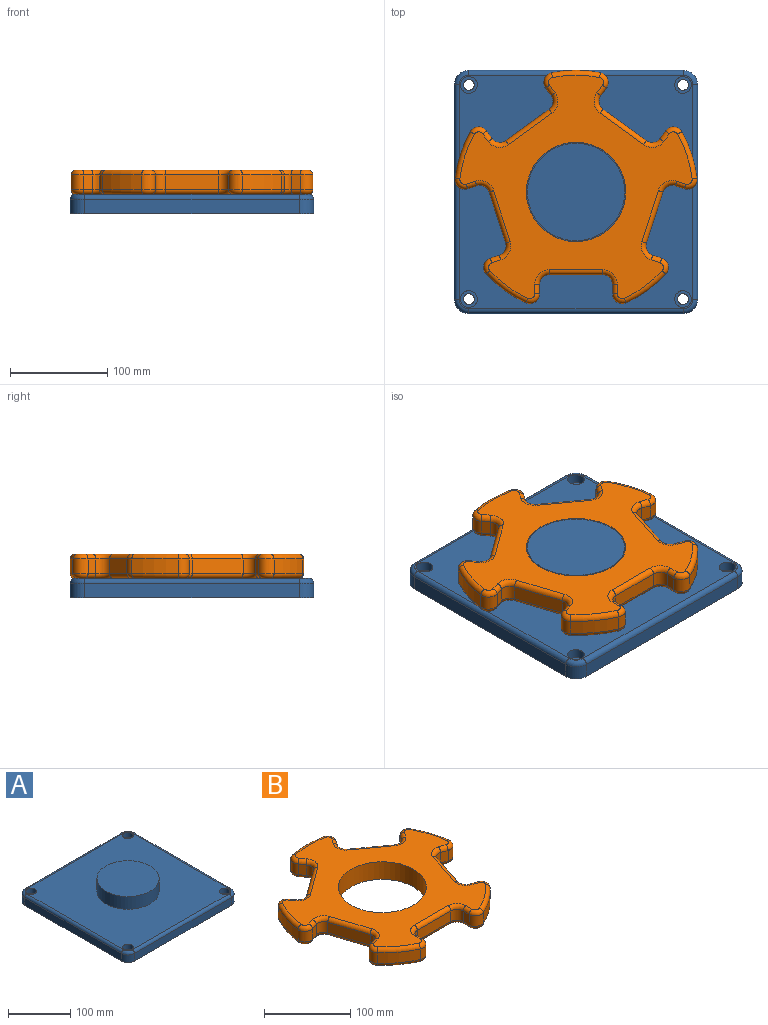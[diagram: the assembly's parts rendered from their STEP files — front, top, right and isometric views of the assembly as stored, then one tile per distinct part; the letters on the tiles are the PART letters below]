
ASSEMBLY  parts=2 mates=1
PART A: 32 faces, bbox 252.5x252.5x45 mm
  f0: plane 220x15mm, normal (1,0,0), area 3300mm2, adj f5,f8,f11,f27
  f1: plane 220x15mm, normal (0,1,0), area 3300mm2, adj f5,f8,f9,f31
  f2: plane 220x15mm, normal (-1,0,0), area 3300mm2, adj f5,f9,f10,f28
  f3: plane 220x15mm, normal (0,-1,0), area 3300mm2, adj f5,f10,f11,f24
  f4: plane 240x240mm, normal (0,0,1), area 48725.4mm2, adj f6,f14,f17,f20,f23,f24,f25,f26
  f5: plane 250x250mm, normal (0,0,-1), area 61926.7mm2, adj f0,f1,f2,f3,f8,f9,f10,f11
  f6: cylinder r=50mm len=100mm, axis (0,0,-1), area 7854mm2, adj f4,f7
  f7: plane 100x100mm, normal (0,0,1), area 7854mm2, adj f6
  f8: cylinder r=15mm len=15mm, axis (0,0,-1), area 353.4mm2, adj f0,f1,f5,f29
  f9: cylinder r=15mm len=15mm, axis (0,0,1), area 353.4mm2, adj f1,f2,f5,f30
  f10: cylinder r=15mm len=15mm, axis (0,0,-1), area 353.4mm2, adj f2,f3,f5,f26
  f11: cylinder r=15mm len=15mm, axis (0,0,1), area 353.4mm2, adj f0,f3,f5,f25
  f12: cylinder r=5.5mm len=11mm, axis (0,0,1), area 345.6mm2, adj f5,f13
  f13: plane 17.25x17.25mm, normal (0,0,1), area 138.7mm2, adj f12,f14
  f14: cylinder r=8.62mm len=17.25mm, axis (0,0,1), area 541.9mm2, adj f4,f13
  f15: cylinder r=5.5mm len=11mm, axis (0,0,1), area 345.6mm2, adj f5,f16
  f16: plane 17.25x17.25mm, normal (0,0,1), area 138.7mm2, adj f15,f17
  f17: cylinder r=8.62mm len=17.25mm, axis (0,0,1), area 541.9mm2, adj f4,f16
  f18: cylinder r=5.5mm len=11mm, axis (0,0,1), area 345.6mm2, adj f5,f19
  f19: plane 17.25x17.25mm, normal (0,0,1), area 138.7mm2, adj f18,f20
  f20: cylinder r=8.62mm len=17.25mm, axis (0,0,1), area 541.9mm2, adj f4,f19
  f21: cylinder r=5.5mm len=11mm, axis (0,0,1), area 345.6mm2, adj f5,f22
  f22: plane 17.25x17.25mm, normal (0,0,1), area 138.7mm2, adj f21,f23
  f23: cylinder r=8.62mm len=17.25mm, axis (0,0,1), area 541.9mm2, adj f4,f22
  f24: cylinder r=5mm len=220mm, axis (-1,0,0), area 1727.9mm2, adj f3,f4,f25,f26
  f25: torus R=10mm, axis (0,0,1), area 162.6mm2, adj f4,f11,f24,f27
  f26: torus R=10mm, axis (0,0,1), area 162.6mm2, adj f4,f10,f24,f28
  f27: cylinder r=5mm len=220mm, axis (0,-1,0), area 1727.9mm2, adj f0,f4,f25,f29
  f28: cylinder r=5mm len=220mm, axis (0,1,0), area 1727.9mm2, adj f2,f4,f26,f30
  f29: torus R=10mm, axis (0,0,1), area 162.6mm2, adj f4,f8,f27,f31
  f30: torus R=10mm, axis (0,0,1), area 162.6mm2, adj f4,f9,f28,f31
  f31: cylinder r=5mm len=220mm, axis (1,0,0), area 1727.9mm2, adj f1,f4,f29,f30
PART B: 123 faces, bbox 268.9x258.5x25 mm
  f0: plane 238.57x229.73mm, normal (0,0,1), area 21505.7mm2, adj f6,f83,f84,f85,f86,f87,f88,f89
  f1: plane 238.57x229.73mm, normal (0,0,-1), area 21505.7mm2, adj f6,f43,f44,f45,f46,f47,f48,f49
  f2: cylinder r=125mm len=47.82mm, axis (0,0,-1), area 759.5mm2, adj f34,f42,f74,f114
  f3: cylinder r=125mm len=50.29mm, axis (0,0,-1), area 759.5mm2, adj f27,f35,f75,f115
  f4: cylinder r=125mm len=47.82mm, axis (0,0,-1), area 759.5mm2, adj f20,f28,f59,f99
  f5: cylinder r=125mm len=40.68mm, axis (0,0,-1), area 759.5mm2, adj f13,f21,f43,f83
  f6: cylinder r=51mm len=102mm, axis (0,0,-1), area 8011.1mm2, adj f0,f1
  f7: cylinder r=125mm len=40.68mm, axis (0,0,-1), area 759.5mm2, adj f14,f41,f58,f98
  f8: plane 15x9.73mm, normal (-1,0,0), area 146mm2, adj f11,f14,f54,f94
  f9: plane 55x15mm, normal (0,-1,0), area 825mm2, adj f11,f12,f50,f90
  f10: plane 15x9.73mm, normal (1,0,0), area 146mm2, adj f12,f13,f46,f86
  f11: cylinder r=10mm len=15mm, axis (0,0,-1), area 235.6mm2, adj f8,f9,f52,f92
  f12: cylinder r=10mm len=15mm, axis (0,0,-1), area 235.6mm2, adj f9,f10,f48,f88
  f13: cylinder r=10mm len=15mm, axis (0,0,-1), area 299.5mm2, adj f5,f10,f44,f84
  f14: cylinder r=10mm len=15mm, axis (0,0,-1), area 299.5mm2, adj f7,f8,f56,f96
  f15: plane 15x9.26mm, normal (-0.31,0.95,0), area 146mm2, adj f18,f21,f47,f87
  f16: plane 52.31x17mm, normal (-0.95,-0.31,0), area 825mm2, adj f18,f19,f51,f91
  f17: plane 15x9.26mm, normal (0.31,-0.95,0), area 146mm2, adj f19,f20,f55,f95
  f18: cylinder r=10mm len=15mm, axis (0,0,-1), area 235.6mm2, adj f15,f16,f49,f89
  f19: cylinder r=10mm len=15mm, axis (0,0,-1), area 235.6mm2, adj f16,f17,f53,f93
  f20: cylinder r=10mm len=15mm, axis (0,0,-1), area 299.5mm2, adj f4,f17,f57,f97
  f21: cylinder r=10mm len=16.25mm, axis (0,0,-1), area 299.5mm2, adj f5,f15,f45,f85
  f22: plane 15x7.87mm, normal (0.81,0.59,0), area 146mm2, adj f25,f28,f63,f103
  f23: plane 44.5x32.33mm, normal (-0.59,0.81,0), area 825mm2, adj f25,f26,f67,f107
  f24: plane 15x7.87mm, normal (-0.81,-0.59,0), area 146mm2, adj f26,f27,f71,f111
  f25: cylinder r=10mm len=15mm, axis (0,0,-1), area 235.6mm2, adj f22,f23,f65,f105
  f26: cylinder r=10mm len=15mm, axis (0,0,-1), area 235.6mm2, adj f23,f24,f69,f109
  f27: cylinder r=10mm len=15.67mm, axis (0,0,-1), area 299.5mm2, adj f3,f24,f73,f113
  f28: cylinder r=10mm len=16.78mm, axis (0,0,-1), area 299.5mm2, adj f4,f22,f61,f101
  f29: plane 15x7.87mm, normal (0.81,-0.59,0), area 146mm2, adj f32,f35,f79,f119
  f30: plane 44.5x32.33mm, normal (0.59,0.81,0), area 825mm2, adj f32,f33,f82,f122
  f31: plane 15x7.87mm, normal (-0.81,0.59,0), area 146mm2, adj f33,f34,f78,f118
  f32: cylinder r=10mm len=15mm, axis (0,0,-1), area 235.6mm2, adj f29,f30,f81,f121
  f33: cylinder r=10mm len=15mm, axis (0,0,-1), area 235.6mm2, adj f30,f31,f80,f120
  f34: cylinder r=10mm len=16.78mm, axis (0,0,-1), area 299.5mm2, adj f2,f31,f76,f116
  f35: cylinder r=10mm len=15.67mm, axis (0,0,-1), area 299.5mm2, adj f3,f29,f77,f117
  f36: plane 15x9.26mm, normal (-0.31,-0.95,0), area 146mm2, adj f39,f42,f70,f110
  f37: plane 52.31x17mm, normal (0.95,-0.31,0), area 825mm2, adj f39,f40,f66,f106
  f38: plane 15x9.26mm, normal (0.31,0.95,0), area 146mm2, adj f40,f41,f62,f102
  f39: cylinder r=10mm len=15mm, axis (0,0,-1), area 235.6mm2, adj f36,f37,f68,f108
  f40: cylinder r=10mm len=15mm, axis (0,0,-1), area 235.6mm2, adj f37,f38,f64,f104
  f41: cylinder r=10mm len=16.25mm, axis (0,0,-1), area 299.5mm2, adj f7,f38,f60,f100
  f42: cylinder r=10mm len=15mm, axis (0,0,-1), area 299.5mm2, adj f2,f36,f72,f112
  f43: torus R=120mm, axis (0,0,1), area 391.9mm2, adj f1,f5,f44,f45
  f44: torus R=5mm, axis (0,0,1), area 128.3mm2, adj f1,f13,f43,f46
  f45: torus R=5mm, axis (0,0,1), area 128.3mm2, adj f1,f21,f43,f47
  f46: cylinder r=5mm len=9.73mm, axis (0,-1,0), area 76.4mm2, adj f1,f10,f44,f48
  f47: cylinder r=5mm len=10.8mm, axis (0.95,0.31,0), area 76.4mm2, adj f1,f15,f45,f49
  f48: torus R=15mm, axis (0,0,1), area 145.8mm2, adj f1,f12,f46,f50
  f49: torus R=15mm, axis (0,0,1), area 145.8mm2, adj f1,f18,f47,f51
  f50: cylinder r=5mm len=55mm, axis (-1,0,0), area 432mm2, adj f1,f9,f48,f52
  f51: cylinder r=5mm len=53.85mm, axis (-0.31,0.95,0), area 432mm2, adj f1,f16,f49,f53
  f52: torus R=15mm, axis (0,0,1), area 145.8mm2, adj f1,f11,f50,f54
  f53: torus R=15mm, axis (0,0,1), area 145.8mm2, adj f1,f19,f51,f55
  f54: cylinder r=5mm len=9.73mm, axis (0,1,0), area 76.4mm2, adj f1,f8,f52,f56
  f55: cylinder r=5mm len=10.8mm, axis (-0.95,-0.31,0), area 76.4mm2, adj f1,f17,f53,f57
  f56: torus R=5mm, axis (0,0,1), area 128.3mm2, adj f1,f14,f54,f58
  f57: torus R=5mm, axis (0,0,1), area 128.3mm2, adj f1,f20,f55,f59
  f58: torus R=120mm, axis (0,0,1), area 391.9mm2, adj f1,f7,f56,f60
  f59: torus R=120mm, axis (0,0,1), area 391.9mm2, adj f1,f4,f57,f61
  f60: torus R=5mm, axis (0,0,1), area 128.3mm2, adj f1,f41,f58,f62
  f61: torus R=5mm, axis (0,0,1), area 128.3mm2, adj f1,f28,f59,f63
  f62: cylinder r=5mm len=10.8mm, axis (0.95,-0.31,0), area 76.4mm2, adj f1,f38,f60,f64
  f63: cylinder r=5mm len=10.81mm, axis (0.59,-0.81,0), area 76.4mm2, adj f1,f22,f61,f65
  f64: torus R=15mm, axis (0,0,1), area 145.8mm2, adj f1,f40,f62,f66
  f65: torus R=15mm, axis (0,0,1), area 145.8mm2, adj f1,f25,f63,f67
  f66: cylinder r=5mm len=53.85mm, axis (-0.31,-0.95,0), area 432mm2, adj f1,f37,f64,f68
  f67: cylinder r=5mm len=47.44mm, axis (0.81,0.59,0), area 432mm2, adj f1,f23,f65,f69
  f68: torus R=15mm, axis (0,0,1), area 145.8mm2, adj f1,f39,f66,f70
  f69: torus R=15mm, axis (0,0,1), area 145.8mm2, adj f1,f26,f67,f71
  f70: cylinder r=5mm len=10.8mm, axis (-0.95,0.31,0), area 76.4mm2, adj f1,f36,f68,f72
  f71: cylinder r=5mm len=10.81mm, axis (-0.59,0.81,0), area 76.4mm2, adj f1,f24,f69,f73
  f72: torus R=5mm, axis (0,0,1), area 128.3mm2, adj f1,f42,f70,f74
  f73: torus R=5mm, axis (0,0,1), area 128.3mm2, adj f1,f27,f71,f75
  f74: torus R=120mm, axis (0,0,1), area 391.9mm2, adj f1,f2,f72,f76
  f75: torus R=120mm, axis (0,0,1), area 391.9mm2, adj f1,f3,f73,f77
  f76: torus R=5mm, axis (0,0,1), area 128.3mm2, adj f1,f34,f74,f78
  f77: torus R=5mm, axis (0,0,1), area 128.3mm2, adj f1,f35,f75,f79
  f78: cylinder r=5mm len=10.81mm, axis (0.59,0.81,0), area 76.4mm2, adj f1,f31,f76,f80
  f79: cylinder r=5mm len=10.81mm, axis (-0.59,-0.81,0), area 76.4mm2, adj f1,f29,f77,f81
  f80: torus R=15mm, axis (0,0,1), area 145.8mm2, adj f1,f33,f78,f82
  f81: torus R=15mm, axis (0,0,1), area 145.8mm2, adj f1,f32,f79,f82
  f82: cylinder r=5mm len=47.44mm, axis (0.81,-0.59,0), area 432mm2, adj f1,f30,f80,f81
  f83: torus R=120mm, axis (0,0,1), area 391.9mm2, adj f0,f5,f84,f85
  f84: torus R=5mm, axis (0,0,1), area 128.3mm2, adj f0,f13,f83,f86
  f85: torus R=5mm, axis (0,0,1), area 128.3mm2, adj f0,f21,f83,f87
  f86: cylinder r=5mm len=9.73mm, axis (0,1,0), area 76.4mm2, adj f0,f10,f84,f88
  f87: cylinder r=5mm len=10.8mm, axis (-0.95,-0.31,0), area 76.4mm2, adj f0,f15,f85,f89
  f88: torus R=15mm, axis (0,0,1), area 145.8mm2, adj f0,f12,f86,f90
  f89: torus R=15mm, axis (0,0,1), area 145.8mm2, adj f0,f18,f87,f91
  f90: cylinder r=5mm len=55mm, axis (1,0,0), area 432mm2, adj f0,f9,f88,f92
  f91: cylinder r=5mm len=53.85mm, axis (0.31,-0.95,0), area 432mm2, adj f0,f16,f89,f93
  f92: torus R=15mm, axis (0,0,1), area 145.8mm2, adj f0,f11,f90,f94
  f93: torus R=15mm, axis (0,0,1), area 145.8mm2, adj f0,f19,f91,f95
  f94: cylinder r=5mm len=9.73mm, axis (0,-1,0), area 76.4mm2, adj f0,f8,f92,f96
  f95: cylinder r=5mm len=10.8mm, axis (0.95,0.31,0), area 76.4mm2, adj f0,f17,f93,f97
  f96: torus R=5mm, axis (0,0,1), area 128.3mm2, adj f0,f14,f94,f98
  f97: torus R=5mm, axis (0,0,1), area 128.3mm2, adj f0,f20,f95,f99
  f98: torus R=120mm, axis (0,0,1), area 391.9mm2, adj f0,f7,f96,f100
  f99: torus R=120mm, axis (0,0,1), area 391.9mm2, adj f0,f4,f97,f101
  f100: torus R=5mm, axis (0,0,1), area 128.3mm2, adj f0,f41,f98,f102
  f101: torus R=5mm, axis (0,0,1), area 128.3mm2, adj f0,f28,f99,f103
  f102: cylinder r=5mm len=10.8mm, axis (-0.95,0.31,0), area 76.4mm2, adj f0,f38,f100,f104
  f103: cylinder r=5mm len=10.81mm, axis (-0.59,0.81,0), area 76.4mm2, adj f0,f22,f101,f105
  f104: torus R=15mm, axis (0,0,1), area 145.8mm2, adj f0,f40,f102,f106
  f105: torus R=15mm, axis (0,0,1), area 145.8mm2, adj f0,f25,f103,f107
  f106: cylinder r=5mm len=53.85mm, axis (0.31,0.95,0), area 432mm2, adj f0,f37,f104,f108
  f107: cylinder r=5mm len=47.44mm, axis (-0.81,-0.59,0), area 432mm2, adj f0,f23,f105,f109
  f108: torus R=15mm, axis (0,0,1), area 145.8mm2, adj f0,f39,f106,f110
  f109: torus R=15mm, axis (0,0,1), area 145.8mm2, adj f0,f26,f107,f111
  f110: cylinder r=5mm len=10.8mm, axis (0.95,-0.31,0), area 76.4mm2, adj f0,f36,f108,f112
  f111: cylinder r=5mm len=10.81mm, axis (0.59,-0.81,0), area 76.4mm2, adj f0,f24,f109,f113
  f112: torus R=5mm, axis (0,0,1), area 128.3mm2, adj f0,f42,f110,f114
  f113: torus R=5mm, axis (0,0,1), area 128.3mm2, adj f0,f27,f111,f115
  f114: torus R=120mm, axis (0,0,1), area 391.9mm2, adj f0,f2,f112,f116
  f115: torus R=120mm, axis (0,0,1), area 391.9mm2, adj f0,f3,f113,f117
  f116: torus R=5mm, axis (0,0,1), area 128.3mm2, adj f0,f34,f114,f118
  f117: torus R=5mm, axis (0,0,1), area 128.3mm2, adj f0,f35,f115,f119
  f118: cylinder r=5mm len=10.81mm, axis (-0.59,-0.81,0), area 76.4mm2, adj f0,f31,f116,f120
  f119: cylinder r=5mm len=10.81mm, axis (0.59,0.81,0), area 76.4mm2, adj f0,f29,f117,f121
  f120: torus R=15mm, axis (0,0,1), area 145.8mm2, adj f0,f33,f118,f122
  f121: torus R=15mm, axis (0,0,1), area 145.8mm2, adj f0,f32,f119,f122
  f122: cylinder r=5mm len=47.44mm, axis (-0.81,0.59,0), area 432mm2, adj f0,f30,f120,f121
PLACE A at identity fixed
PLACE B at identity
MATE revolute B.f2 <-> A.f6  axis (0,0,1) through (0,0,45)mm
